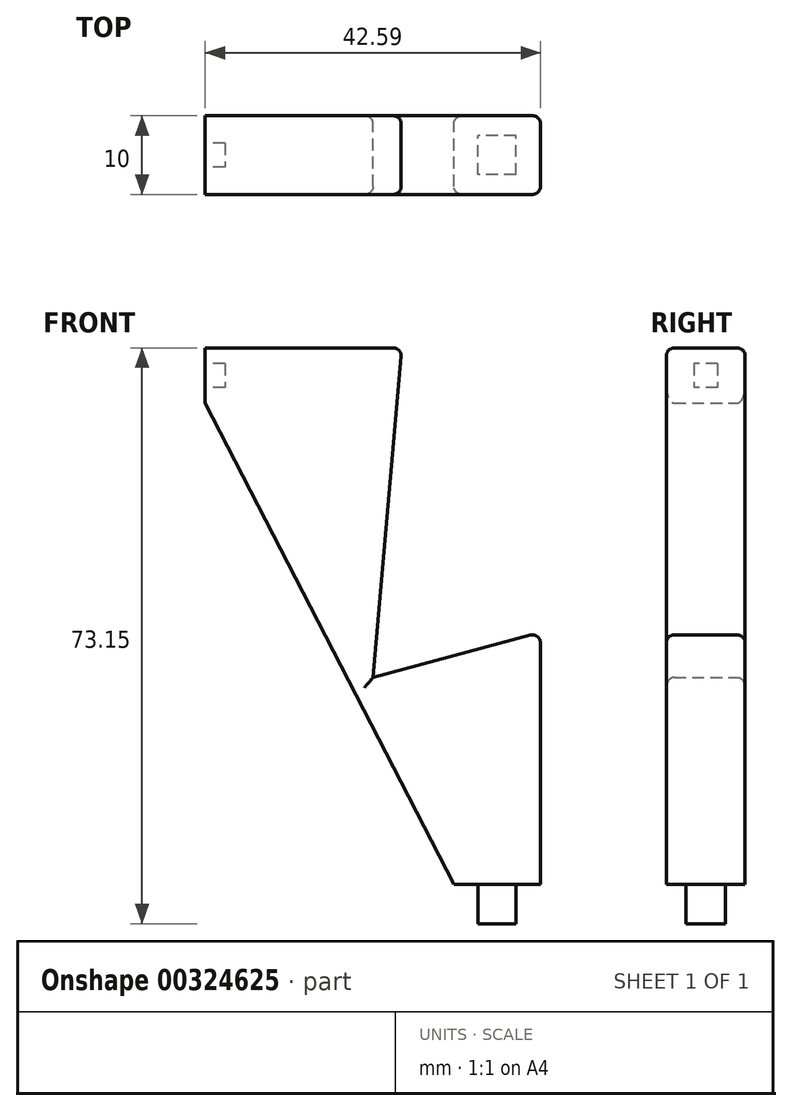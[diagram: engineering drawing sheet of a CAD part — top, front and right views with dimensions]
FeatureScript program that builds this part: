
annotation { "Feature Type Name" : "Feature", "Feature Type Description" : "" }
export const myFeature = defineFeature(function(context is Context, id is Id, definition is map)
    precondition{}
    {
        {
            var Q0;
            Q0=qCreatedBy(makeId("Front.planeOp"),FACE);
            var sketch = newSketch(context, id + "F0", { "sketchPlane" : qUnion([Q0])});
            skLineSegment(sketch, "E0", {"start": v(0, 0) * mm, "end": v(25, 0) * mm});
            skLineSegment(sketch, "E1", {"start": v(25, 0) * mm, "end": v(21.34, -41.84) * mm});
            skLineSegment(sketch, "E2", {"start": v(21.34, -41.84) * mm, "end": v(42.59, -36.15) * mm});
            skLineSegment(sketch, "E3", {"start": v(42.59, -36.15) * mm, "end": v(42.59, -68.15) * mm});
            skLineSegment(sketch, "E4", {"start": v(42.59, -68.15) * mm, "end": v(31.59, -68.15) * mm});
            skLineSegment(sketch, "E5", {"start": v(0, 0) * mm, "end": v(0, -7) * mm});
            skLineSegment(sketch, "E6", {"start": v(0, -7) * mm, "end": v(31.59, -68.15) * mm});
            skSolve(sketch);
        }
        {
            var Q0;
            Q0=makeQuery(id+"F0.imprint","IMPRINT",FACE,{"disambiguationData":[TD([[makeQuery(id+"F0.imprint","IMPRINT",EDGE,{"derivedFrom":sQuery(id+"F0.wireOp",EDGE,"E0")}),-1.0]])]});
            extrude(context, id + "F1", {"entities" : qUnion([Q0]), "depth" : 10 * mm});
        }
        {
            var Q0;
            Q0=makeQuery(id+"F1.opExtrude","SWEPT_FACE",FACE,{"disambiguationData":[OSD([sQuery(id+"F0.wireOp",EDGE,"E4")])]});
            var sketch = newSketch(context, id + "F2", { "sketchPlane" : qUnion([Q0])});
            skLineSegment(sketch, "E7.bottom", {"start": v(39.49, 7.5) * mm, "end": v(34.69, 7.5) * mm});
            skLineSegment(sketch, "E7.top", {"start": v(39.49, 2.5) * mm, "end": v(34.69, 2.5) * mm});
            skLineSegment(sketch, "E7.left", {"start": v(39.49, 7.5) * mm, "end": v(39.49, 2.5) * mm});
            skLineSegment(sketch, "E7.right", {"start": v(34.69, 7.5) * mm, "end": v(34.69, 2.5) * mm});
            skPoint(sketch, "E7.middle", {"position": v(37.09, 5) * mm});
            skPoint(sketch, "E7.middle.positionSnap0", {"position": v(37.09, 7.5) * mm});
            skPoint(sketch, "E7.middle.positionSnap1", {"position": v(31.59, 5) * mm});
            skPoint(sketch, "E7.centerSnap0", {"position": v(37.09, 7.5) * mm});
            skPoint(sketch, "E7.centerSnap1", {"position": v(31.59, 5) * mm});
            skSolve(sketch);
        }
        {
            var Q0;
            Q0=makeQuery(id+"F2.imprint","IMPRINT",FACE,{"disambiguationData":[TD([[makeQuery(id+"F2.imprint","IMPRINT",EDGE,{"derivedFrom":sQuery(id+"F2.wireOp",EDGE,"E7.bottom")}),1.0]])]});
            var sketch = newSketch(context, id + "F3", { "sketchPlane" : qUnion([Q0])});
            skSolve(sketch);
        }
        {
            var Q0;
            Q0=makeQuery(id+"F3.imprint","IMPRINT",FACE,{"disambiguationData":[TD([[makeQuery(id+"F3.imprint","IMPRINT",EDGE,{"derivedFrom":makeQuery(id+"F2.imprint","IMPRINT",EDGE,{"derivedFrom":sQuery(id+"F2.wireOp",EDGE,"E7.bottom")})}),1.0]])]});
            extrude(context, id + "F4", {"entities" : qUnion([Q0]), "operationType" : NewBodyOperationType.ADD, "depth" : 5 * mm});
        }
        {
            var Q0;
            Q0=makeQuery(id+"F1.opExtrude","SWEPT_FACE",FACE,{"disambiguationData":[OSD([sQuery(id+"F0.wireOp",EDGE,"E5")])]});
            var sketch = newSketch(context, id + "F5", { "sketchPlane" : qUnion([Q0])});
            skLineSegment(sketch, "E8.bottom", {"start": v(3.5, -2) * mm, "end": v(6.5, -2) * mm});
            skLineSegment(sketch, "E8.top", {"start": v(3.5, -5) * mm, "end": v(6.5, -5) * mm});
            skLineSegment(sketch, "E8.left", {"start": v(3.5, -2) * mm, "end": v(3.5, -5) * mm});
            skLineSegment(sketch, "E8.right", {"start": v(6.5, -2) * mm, "end": v(6.5, -5) * mm});
            skPoint(sketch, "E8.middle", {"position": v(5, -3.5) * mm});
            skPoint(sketch, "E8.middle.positionSnap0", {"position": v(0, -3.5) * mm});
            skPoint(sketch, "E8.middle.positionSnap1", {"position": v(5, 0) * mm});
            skPoint(sketch, "E8.centerSnap0", {"position": v(0, -3.5) * mm});
            skPoint(sketch, "E8.centerSnap1", {"position": v(5, 0) * mm});
            skSolve(sketch);
        }
        {
            var Q0;
            Q0=makeQuery(id+"F5.imprint","IMPRINT",FACE,{"disambiguationData":[TD([[makeQuery(id+"F5.imprint","IMPRINT",EDGE,{"derivedFrom":sQuery(id+"F5.wireOp",EDGE,"E8.bottom")}),-1.0]])]});
            extrude(context, id + "F6", {"entities" : qUnion([Q0]), "operationType" : NewBodyOperationType.REMOVE, "oppositeDirection" : true, "depth" : 2.5 * mm});
        }
        {
            var Q0;
            Q0=makeQuery(id+"F1.opExtrude","CAP_EDGE",EDGE,{"disambiguationData":[OSD([sQuery(id+"F0.wireOp",EDGE,"E1")])],"isStart":false});
            fillet(context, id + "F7", {"entities" : qUnion([Q0]), "radius" : 1 * mm, "tangentPropagation" : true, "allowEdgeOverflow" : false});
        }
        {
            var Q0;
            Q0=makeQuery(id+"F1.opExtrude","CAP_EDGE",EDGE,{"disambiguationData":[OSD([sQuery(id+"F0.wireOp",EDGE,"E1")])],"isStart":true});
            fillet(context, id + "F8", {"entities" : qUnion([Q0]), "radius" : 1 * mm, "tangentPropagation" : true, "allowEdgeOverflow" : false});
        }
        {
            var Q0;
            Q0=makeQuery(id+"F1.opExtrude","CAP_EDGE",EDGE,{"disambiguationData":[OSD([sQuery(id+"F0.wireOp",EDGE,"E6")])],"isStart":true});
            var Q1;
            Q1=makeQuery(id+"F1.opExtrude","CAP_EDGE",EDGE,{"disambiguationData":[OSD([sQuery(id+"F0.wireOp",EDGE,"E6")])],"isStart":false});
            fillet(context, id + "F9", {"entities" : qUnion([Q0, Q1]), "radius" : 1 * mm, "tangentPropagation" : true, "allowEdgeOverflow" : false});
        }
        {
            var Q0;
            Q0=makeQuery(id+"F1.opExtrude","CAP_EDGE",EDGE,{"disambiguationData":[OSD([sQuery(id+"F0.wireOp",EDGE,"E2")])],"isStart":true});
            fillet(context, id + "F10", {"entities" : qUnion([Q0]), "radius" : 1 * mm, "tangentPropagation" : true, "allowEdgeOverflow" : false});
        }
        {
            var Q0;
            Q0=makeQuery(id+"F1.opExtrude","CAP_EDGE",EDGE,{"disambiguationData":[OSD([sQuery(id+"F0.wireOp",EDGE,"E2")])],"isStart":false});
            fillet(context, id + "F11", {"entities" : qUnion([Q0]), "radius" : 1 * mm, "tangentPropagation" : true, "allowEdgeOverflow" : false});
        }
        {
            var Q0;
            Q0=makeQuery(id+"F1.opExtrude","CAP_EDGE",EDGE,{"disambiguationData":[OSD([sQuery(id+"F0.wireOp",EDGE,"E3")])],"isStart":true});
            fillet(context, id + "F12", {"entities" : qUnion([Q0]), "radius" : 1 * mm, "tangentPropagation" : true, "allowEdgeOverflow" : false});
        }
        {
            var Q0;
            Q0=makeQuery(id+"F1.opExtrude","CAP_EDGE",EDGE,{"disambiguationData":[OSD([sQuery(id+"F0.wireOp",EDGE,"E0")])],"isStart":false});
            fillet(context, id + "F13", {"entities" : qUnion([Q0]), "radius" : 1 * mm, "tangentPropagation" : true, "allowEdgeOverflow" : false});
        }
    });
